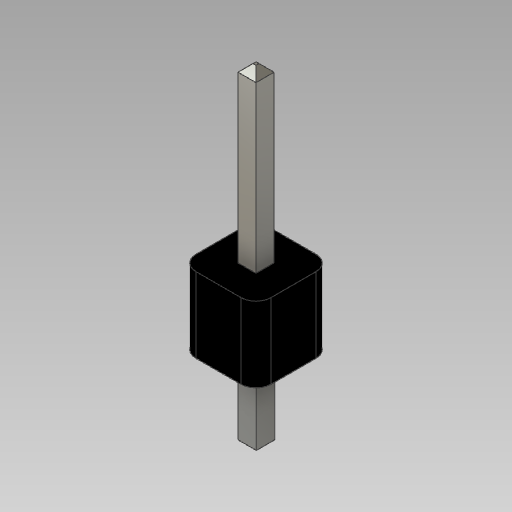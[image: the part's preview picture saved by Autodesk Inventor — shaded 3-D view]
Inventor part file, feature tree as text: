
AUTODESK INVENTOR PART (.ipt)
format: ipt  version: 2020 (Build 240168000, 168)  size: 605,184 bytes
history: native  units: in
note: dims shown in document units (in); Inventor stores cm internally (conversion verified against a paired STEP export)
features: other x5, sketch x5, extrude x4, chamfer x2
ambient origin geometry x8: Origin, YZ Plane, XZ Plane, XY Plane, X Axis, Y Axis, Z Axis, Center Point
bodies: Solid1 (feature_tree)
feature tree (16):
  extrude  "Extrusion1"  Depth=0.02in
  extrude  "Extrusion2"  Depth=0.1in TaperAngle=0.0deg
  chamfer  "Chamfer2"  Distance=0.23in
  extrude  "Extrusion3"  Depth=0.1in
  chamfer  "Chamfer4"  Distance=0.114in
  other  "Work Point1"
  other  "Work Point2"
  other  "Work Axis1"
  other  "Work Axis2"
  extrude  "Extrusion4"  Depth=0.114in TaperAngle=45.0deg
  sketch  "Sketch10"  dims[d26=0.01in d27=0.125in d28=45.0deg d29=6.2992in d31=0.1in d32=0.3937in d34=1.0in d36=0.114in d37=0.0in d41=0.01in d42=0.125in d43=45.0deg d46=0.0in d47=0.0in]
  other  "Work Axis3"
  sketch  "Sketch1"  dims[d0=0.1in d1=0.02in]
  sketch  "Sketch2"  dims[d2=6.2992in d4=0.1in d5=0.3937in d7=1.0in d9=0.1in d10=0.0in]
  sketch  "Sketch6"  dims[d11=0.024in]
  sketch  "Sketch9"  dims[d12=6.2992in d14=0.1in d15=0.3937in d17=1.0in d19=0.23in d20=0.0in]
